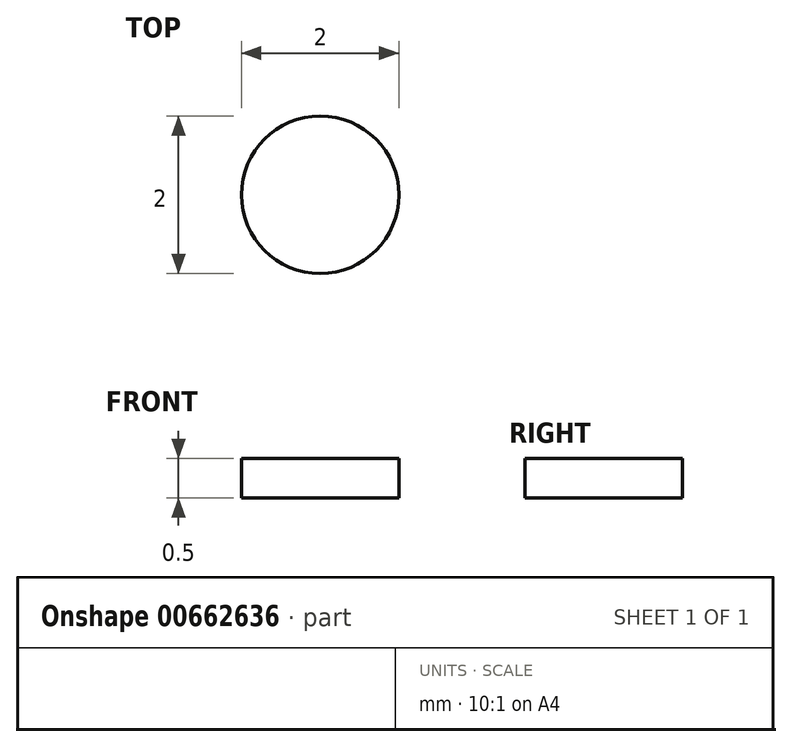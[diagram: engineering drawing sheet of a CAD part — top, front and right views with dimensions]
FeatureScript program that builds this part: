
annotation { "Feature Type Name" : "Feature", "Feature Type Description" : "" }
export const myFeature = defineFeature(function(context is Context, id is Id, definition is map)
    precondition{}
    {
        {
            var Q0;
            Q0=qCreatedBy(makeId("Top.planeOp"),FACE);
            var sketch = newSketch(context, id + "F0", { "sketchPlane" : qUnion([Q0])});
            skCircle(sketch, "E0", {"center": v(0, 0) * mm, "radius": 1 * mm});
            skSolve(sketch);
        }
        {
            var Q0;
            Q0=makeQuery(id+"F0.imprint","IMPRINT",FACE,{"disambiguationData":[TD([[makeQuery(id+"F0.imprint","IMPRINT",EDGE,{"derivedFrom":sQuery(id+"F0.wireOp",EDGE,"E0")}),1.0]])]});
            extrude(context, id + "F1", {"entities" : qUnion([Q0]), "depth" : .5 * mm, "offsetDistance" : 25 * mm});
        }
    });
